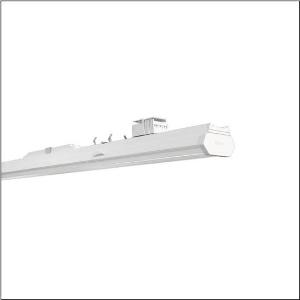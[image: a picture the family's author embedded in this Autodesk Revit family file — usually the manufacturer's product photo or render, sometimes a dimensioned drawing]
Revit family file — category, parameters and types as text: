
# Revit family: licross_21_protected_ho_52tp12cn4cxm
name_source: partatom
category: Lighting Fixtures
units: mm (PartAtom-declared; Revit-internal decimal feet)

## family parameters
Cut with Voids When Loaded = No
Host = Face
Light Source = No
Part Type = Normal
Room Calculation Point = No
Round Connector Dimension = Use Diameter
Shared = No

## types (1)
- --- (1 x LED, 12460 lm, 68.9 W, 4000K)
    Apparent Load = 69 VA
    CIE Flux Codes = 70 91 97 98 100
    Color Rendering = 80
    Color Temperature = 4000K
    Default Elevation = 1800 mm
    Description = Licross 21 Protected HO, luminaire insert, of sheet steel, galvanised, coil coated, white, length: 1.500mm, width: 90mm, height: 103mm, LED rated luminous flux: 12.460lm, light colour: 840, SDCM (Standard Deviation of Colour Matching)MacAdam ≤ 3 SDCM (initial), control gear: ON/OFF Multilumen, CLOi, with plug, 3-pole, with phase selection, mains connection: 220..240V, AC, 50/60Hz, start of lifetime: 69W, end of service life: 83W, internal wiring halogen-free, primary light control with lens, of plastic, primary optical cover: cover, of PMMA, light emission: direct distribution, primary light characteristic: symmetric, protection rating (complete): IP64, insulation class (complete): insulation class I (protective earthing), certification: CE, ENEC, VDE, UKCA, protection symbol: D if used in an environment with conductive dust loads with corresponding accessories, impact resistance: IK06, permissible ambient temperature for indoor applications: -35..+35°C, corresponds to IFS (International Featured Standards) requirements for safety and quality in the food industry, reducing of maximum allowable ambient temperature of 5°C with ceiling mounting, LABS conformity tested according to VDMA 24364:2018-05, The light source and the operating device comply with the requirements of the Ecodesign Regulation (EU) 2019/2020 and are replaceable in accordance with this regulation, packaging unit: 1 piece
    Height = 92 mm
    Lamp = 1 x LED
    Lamp Light Flux = 12460 lm
    Lamp Power = 68.9 W
    Lamp count = 1
    Length = 1500 mm
    Luminous efficacy = 181 lm/W
    Manufacturer = Siteco
    ModVariant = No
    Model = 52TP12CN4CXM
    Mounting Place = Ceiling
    Mounting Type = Pendant
    Number of Poles = 1
    OnlyDefault = Yes
    Power Factor = 1
    Product Name = Licross 21 Protected HO
    Product group = luminaire insert | ceiling pendant
    ProductGroupID = 901
    Protection Class = Protection class I
    Protection Degree = IP 64
    RLX_Detail_Level = 1
    RLX_Emergency_Light_Flux = 0 lm
    RLX_Emergency_Type = 0
    RLX_Emergency_Type_DB = No
    RlxData = <blob elided: 22401 chars, md5=1af2fc93>
    Socket = socket
    Standby Power = 0 W
    System Light Flux = 12460 lm
    System Power = 69 W
    Type Comments = factory setting: luminous flux: 100 % | (A | C | E) | 162 mA
    Type Image = l_1256148.jpg
    URL = http://relux.com
    VarID = @adj_112989
    Voltage = 0 V
    Weight = 0.00 kg
    Width = 88 mm

## geometry (parser evidence)
native form markers: Blend x4, Sweep x11
no freeform markers — native parametric forms only
